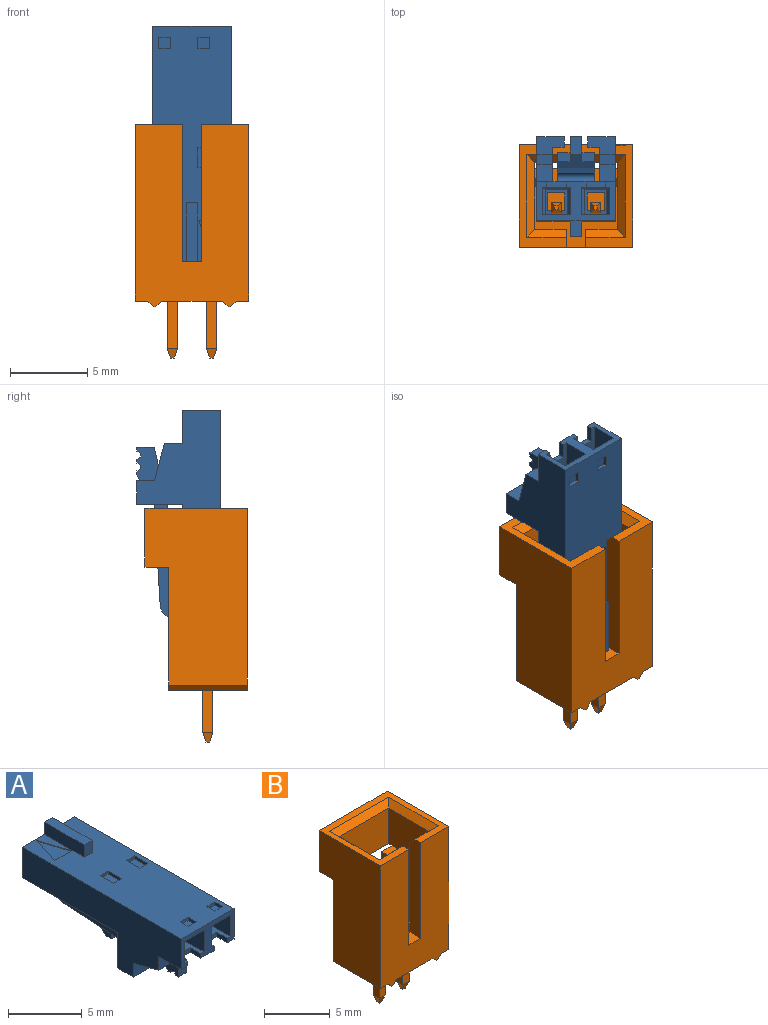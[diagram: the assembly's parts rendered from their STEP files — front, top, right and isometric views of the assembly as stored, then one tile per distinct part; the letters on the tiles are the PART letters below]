
ASSEMBLY  parts=2 mates=1
PART A: 129 faces, bbox 5.1x15.2x6.5 mm
  f0: plane 5.05x2.51mm, normal (0,-1,0), area 5.2mm2, adj f1,f2,f3,f4,f5,f32,f33,f34
  f1: plane 1.02x0.37mm, normal (1,0,0), area 0.4mm2, adj f0,f2,f38,f86
  f2: plane 8.38x1.85mm, normal (0,0,1), area 14.3mm2, adj f0,f1,f3,f5,f7,f86,f87
  f3: plane 8.38x1.78mm, normal (1,0,0), area 14.9mm2, adj f0,f2,f4,f8
  f4: plane 8.38x1.85mm, normal (0,0,-1), area 15.5mm2, adj f0,f3,f5,f9
  f5: plane 8.38x1.78mm, normal (-1,0,0), area 14.9mm2, adj f0,f2,f4,f6
  f6: plane 1.78x0.25mm, normal (-0.76,-0.65,0), area 0.6mm2, adj f5,f7,f9,f11
  f7: plane 1.85x0.25mm, normal (0,-0.29,0.96), area 0.4mm2, adj f2,f6,f8,f12
  f8: plane 1.78x0.25mm, normal (0.76,-0.65,0), area 0.6mm2, adj f3,f7,f9,f13
  f9: plane 1.85x0.25mm, normal (0,-0.29,-0.96), area 0.4mm2, adj f4,f6,f8,f10
  f10: plane 5.79x1.42mm, normal (0,0,-1), area 8.2mm2, adj f9,f11,f13,f14
  f11: plane 5.79x1.63mm, normal (-1,0,0), area 9.4mm2, adj f6,f10,f12,f14
  f12: plane 5.79x1.42mm, normal (0,0,1), area 8.2mm2, adj f7,f11,f13,f14
  f13: plane 5.79x1.63mm, normal (1,0,0), area 9.4mm2, adj f8,f10,f12,f14
  f14: plane 1.63x1.42mm, normal (0,-1,0), area 1.1mm2, adj f10,f11,f12,f13,f15,f16,f17,f18
  f15: plane 1.12x0.46mm, normal (1,0,0), area 0.5mm2, adj f14,f16,f18,f21
  f16: plane 1.12x0.46mm, normal (0,0,-1), area 0.5mm2, adj f14,f15,f17,f22
  f17: plane 1.12x0.46mm, normal (-1,0,0), area 0.5mm2, adj f14,f16,f18,f23
  f18: plane 1.12x0.46mm, normal (0,0,1), area 0.5mm2, adj f14,f15,f17,f19
  f19: plane 1.83x0.36mm, normal (0,0.71,0.71), area 0.7mm2, adj f18,f20,f21,f23
  f20: plane 5.05x3.53mm, normal (0,1,0), area 6.8mm2, adj f19,f21,f22,f23,f24,f25,f26,f27
  f21: plane 1.83x0.36mm, normal (0.71,0.71,0), area 0.7mm2, adj f15,f19,f20,f22
  f22: plane 1.83x0.36mm, normal (0,0.71,-0.71), area 0.7mm2, adj f16,f20,f21,f23
  f23: plane 1.83x0.36mm, normal (-0.71,0.71,0), area 0.7mm2, adj f17,f19,f20,f22
  f24: plane 1.83x0.36mm, normal (0.71,0.71,0), area 0.7mm2, adj f20,f25,f27,f126
  f25: plane 1.83x0.36mm, normal (0,0.71,0.71), area 0.7mm2, adj f20,f24,f26,f127
  f26: plane 1.83x0.36mm, normal (-0.71,0.71,0), area 0.7mm2, adj f20,f25,f27,f128
  f27: plane 1.83x0.36mm, normal (0,0.71,-0.71), area 0.7mm2, adj f20,f24,f26,f28
  f28: plane 1.12x0.46mm, normal (0,0,-1), area 0.5mm2, adj f27,f29,f126,f128
  f29: plane 1.63x1.42mm, normal (0,-1,0), area 1.1mm2, adj f28,f30,f121,f122,f125,f126,f127,f128
  f30: plane 5.79x1.63mm, normal (1,0,0), area 9.4mm2, adj f29,f31,f121,f125
  f31: plane 1.78x0.25mm, normal (0.76,-0.65,0), area 0.6mm2, adj f30,f32,f120,f124
  f32: plane 8.38x1.78mm, normal (1,0,0), area 14.9mm2, adj f0,f31,f33,f35
  f33: plane 8.38x1.85mm, normal (0,0,-1), area 15.5mm2, adj f0,f32,f34,f124
  f34: plane 8.38x1.78mm, normal (-1,0,0), area 14.9mm2, adj f0,f33,f35,f123
  f35: plane 8.38x1.85mm, normal (0,0,1), area 14.3mm2, adj f0,f32,f34,f36,f37,f88,f120
  f36: plane 1.02x0.37mm, normal (1,0,0), area 0.4mm2, adj f0,f35,f37,f38
  f37: plane 1.27x0.37mm, normal (0,-1,0), area 0.5mm2, adj f35,f36,f38,f88
  f38: plane 15.24x5.05mm, normal (0,0,-1), area 63.2mm2, adj f0,f1,f20,f36,f37,f39,f41,f45
  f39: plane 3.94x2.24mm, normal (1,0,0), area 6.9mm2, adj f38,f40,f41,f43,f46,f47
  f40: plane 1.52x0.77mm, normal (0,0,1), area 1.2mm2, adj f39,f41,f43,f44
  f41: plane 2.92x1.77mm, normal (0,1,0), area 3.4mm2, adj f38,f39,f40,f42,f44,f45
  f42: plane 1.77x1.52mm, normal (0,0,-1), area 2.7mm2, adj f41,f43,f44,f45
  f43: plane 1.77x1.14mm, normal (0,-1,0), area 1.7mm2, adj f39,f40,f42,f44,f45,f47
  f44: plane 1.52x0.69mm, normal (1,0,0), area 1mm2, adj f40,f41,f42,f43
  f45: plane 15.24x5.44mm, normal (-1,0,0), area 46.3mm2, adj f0,f20,f38,f41,f42,f43,f46,f47
  f46: plane 1.14x0.99mm, normal (0,-1,0), area 1.1mm2, adj f38,f39,f45,f47
  f47: plane 2.41x0.99mm, normal (0,-0.25,-0.97), area 2.5mm2, adj f39,f43,f45,f46
  f48: plane 15.24x5.05mm, normal (0,0,1), area 69mm2, adj f0,f20,f45,f49,f50,f51,f52,f55
  f49: plane 0.76x0.25mm, normal (0,1,0), area 0.2mm2, adj f48,f50,f52,f53
  f50: plane 1.27x0.25mm, normal (1,0,0), area 0.3mm2, adj f48,f49,f51,f53
  f51: plane 0.76x0.25mm, normal (0,-1,0), area 0.2mm2, adj f48,f50,f52,f53
  f52: plane 1.27x0.25mm, normal (-1,0,0), area 0.3mm2, adj f48,f49,f51,f53
  f53: plane 1.27x0.76mm, normal (0,0,1), area 1mm2, adj f49,f50,f51,f52
  f54: plane 0.76x0.76mm, normal (0,0,1), area 0.6mm2, adj f55,f56,f57,f58
  f55: plane 0.76x0.25mm, normal (0,1,0), area 0.2mm2, adj f48,f54,f56,f58
  f56: plane 0.76x0.25mm, normal (1,0,0), area 0.2mm2, adj f48,f54,f55,f57
  f57: plane 0.76x0.25mm, normal (0,-1,0), area 0.2mm2, adj f48,f54,f56,f58
  f58: plane 0.76x0.25mm, normal (-1,0,0), area 0.2mm2, adj f48,f54,f55,f57
  f59: plane 0.76x0.25mm, normal (0,1,0), area 0.2mm2, adj f48,f60,f62,f63
  f60: plane 1.27x0.25mm, normal (1,0,0), area 0.3mm2, adj f48,f59,f61,f63
  f61: plane 0.76x0.25mm, normal (0,-1,0), area 0.2mm2, adj f48,f60,f62,f63
  f62: plane 1.27x0.25mm, normal (-1,0,0), area 0.3mm2, adj f48,f59,f61,f63
  f63: plane 1.27x0.76mm, normal (0,0,1), area 1mm2, adj f59,f60,f61,f62
  f64: plane 0.76x0.76mm, normal (0,0,1), area 0.6mm2, adj f65,f66,f67,f68
  f65: plane 0.76x0.25mm, normal (0,1,0), area 0.2mm2, adj f48,f64,f66,f68
  f66: plane 0.76x0.25mm, normal (1,0,0), area 0.2mm2, adj f48,f64,f65,f67
  f67: plane 0.76x0.25mm, normal (0,-1,0), area 0.2mm2, adj f48,f64,f66,f68
  f68: plane 0.76x0.25mm, normal (-1,0,0), area 0.2mm2, adj f48,f64,f65,f67
  f69: plane 3.81x1.02mm, normal (1,0,0), area 3.9mm2, adj f20,f48,f70,f72
  f70: plane 1.02x0.76mm, normal (0,-1,0), area 0.8mm2, adj f48,f69,f71,f72
  f71: plane 3.81x1.02mm, normal (-1,0,0), area 3.9mm2, adj f20,f48,f70,f72
  f72: plane 3.81x0.76mm, normal (0,0,1), area 2.9mm2, adj f20,f69,f70,f71
  f73: plane 15.24x5.44mm, normal (1,0,0), area 46.3mm2, adj f0,f20,f38,f48,f74,f77,f78,f80
  f74: plane 2.92x1.77mm, normal (0,1,0), area 3.4mm2, adj f38,f73,f75,f76,f78,f79
  f75: plane 3.94x2.24mm, normal (-1,0,0), area 6.9mm2, adj f38,f74,f76,f77,f80,f81
  f76: plane 1.52x0.77mm, normal (0,0,1), area 1.2mm2, adj f74,f75,f77,f79
  f77: plane 1.77x1.14mm, normal (0,-1,0), area 1.7mm2, adj f73,f75,f76,f78,f79,f80
  f78: plane 1.77x1.52mm, normal (0,0,-1), area 2.7mm2, adj f73,f74,f77,f79
  f79: plane 1.52x0.69mm, normal (-1,0,0), area 1mm2, adj f74,f76,f77,f78
  f80: plane 2.41x0.99mm, normal (0,-0.25,-0.97), area 2.5mm2, adj f73,f75,f77,f81
  f81: plane 1.14x0.99mm, normal (0,-1,0), area 1.1mm2, adj f38,f73,f75,f80
  f82: plane 2.54x0.81mm, normal (0.95,-0.3,0), area 0.1mm2, adj f48,f83,f84,f85
  f83: plane 2.54x0.81mm, normal (-0.95,-0.3,0), area 0.1mm2, adj f48,f82,f84,f85
  f84: plane 1.63x0.05mm, normal (0,1,0), area 0.1mm2, adj f48,f82,f83,f85
  f85: plane 2.54x1.63mm, normal (0,0,1), area 2.1mm2, adj f82,f83,f84
  f86: plane 1.27x0.37mm, normal (0,-1,0), area 0.5mm2, adj f1,f2,f38,f87
  f87: plane 1.02x0.37mm, normal (-1,0,0), area 0.4mm2, adj f0,f2,f38,f86
  f88: plane 1.02x0.37mm, normal (-1,0,0), area 0.4mm2, adj f0,f35,f37,f38
  f89: plane 8.84x1.89mm, normal (-1,0,0), area 7.8mm2, adj f38,f90,f92,f94,f110,f111,f113,f114
  f90: plane 8.07x2.44mm, normal (0,0.06,-1), area 16.1mm2, adj f89,f91,f92,f93,f95,f96,f112,f114
  f91: plane 3.68x1.62mm, normal (-1,0,0), area 4.4mm2, adj f90,f92,f94,f96,f97,f98,f99,f100
  f92: plane 0.84x0.58mm, normal (0,-1,0), area 0.5mm2, adj f89,f90,f91,f94
  f93: plane 0.84x0.58mm, normal (0,-1,0), area 0.5mm2, adj f90,f94,f95,f112
  f94: plane 3.68x2.44mm, normal (0,-0.22,0.98), area 5.5mm2, adj f89,f91,f92,f93,f95,f109,f110,f112
  f95: plane 3.68x1.62mm, normal (1,0,0), area 4.4mm2, adj f90,f93,f94,f96,f97,f98,f99,f100
  f96: plane 1.12x0.76mm, normal (0,1,0), area 0.9mm2, adj f90,f91,f95,f97
  f97: plane 1.52x0.76mm, normal (0,0,-1), area 1.2mm2, adj f91,f95,f96,f98
  f98: plane 0.76x0.19mm, normal (0,-1,0), area 0.1mm2, adj f91,f95,f97,f99
  f99: plane 0.76x0.38mm, normal (0,0.45,-0.89), area 0.3mm2, adj f91,f95,f98,f100
  f100: plane 0.76x0.25mm, normal (0,0,-1), area 0.2mm2, adj f91,f95,f99,f101
  f101: plane 0.76x0.25mm, normal (0,-0.89,-0.45), area 0.2mm2, adj f91,f95,f100,f102
  f102: plane 0.76x0.25mm, normal (0,0,-1), area 0.2mm2, adj f91,f95,f101,f103
  f103: plane 0.76x0.25mm, normal (0,0.89,-0.45), area 0.2mm2, adj f91,f95,f102,f104
  f104: plane 0.76x0.25mm, normal (0,0,-1), area 0.2mm2, adj f91,f95,f103,f105
  f105: plane 0.76x0.25mm, normal (0,-0.89,-0.45), area 0.2mm2, adj f91,f95,f104,f106
  f106: plane 0.76x0.25mm, normal (0,0,-1), area 0.2mm2, adj f91,f95,f105,f107
  f107: plane 0.76x0.25mm, normal (0,0.89,-0.45), area 0.2mm2, adj f91,f95,f106,f108
  f108: plane 0.76x0.25mm, normal (0,0,-1), area 0.2mm2, adj f91,f95,f107,f109
  f109: plane 1.13x0.76mm, normal (0,-1,0), area 0.9mm2, adj f91,f94,f95,f108
  f110: plane 5.94x2.44mm, normal (0,-0.06,1), area 14.5mm2, adj f89,f94,f111,f112
  f111: cylinder r=0.3mm len=2.44mm, axis (1,0,0), area 2.3mm2, adj f38,f89,f110,f112
  f112: plane 8.84x1.89mm, normal (1,0,0), area 7.8mm2, adj f38,f90,f93,f94,f110,f111,f113,f114
  f113: plane 2.44x0.6mm, normal (0,1,0), area 1.5mm2, adj f38,f89,f112,f114
  f114: cylinder r=0.81mm len=2.44mm, axis (1,0,0), area 3mm2, adj f89,f90,f112,f113
  f115: plane 2.03x0.64mm, normal (0,-1,0), area 1.3mm2, adj f90,f116,f118,f119
  f116: plane 1.22x0.71mm, normal (1,0,0), area 0.6mm2, adj f90,f115,f117,f119
  f117: plane 2.03x0.71mm, normal (0,0.73,-0.68), area 2mm2, adj f90,f116,f118,f119
  f118: plane 1.22x0.71mm, normal (-1,0,0), area 0.6mm2, adj f90,f115,f117,f119
  f119: plane 2.03x0.56mm, normal (0,0,-1), area 1.1mm2, adj f115,f116,f117,f118
  f120: plane 1.85x0.25mm, normal (0,-0.29,0.96), area 0.4mm2, adj f31,f35,f121,f123
  f121: plane 5.79x1.42mm, normal (0,0,1), area 8.2mm2, adj f29,f30,f120,f122
  f122: plane 5.79x1.63mm, normal (-1,0,0), area 9.4mm2, adj f29,f121,f123,f125
  f123: plane 1.78x0.25mm, normal (-0.76,-0.65,0), area 0.6mm2, adj f34,f120,f122,f124
  f124: plane 1.85x0.25mm, normal (0,-0.29,-0.96), area 0.4mm2, adj f31,f33,f123,f125
  f125: plane 5.79x1.42mm, normal (0,0,-1), area 8.2mm2, adj f29,f30,f122,f124
  f126: plane 1.12x0.46mm, normal (1,0,0), area 0.5mm2, adj f24,f28,f29,f127
  f127: plane 1.12x0.46mm, normal (0,0,1), area 0.5mm2, adj f25,f29,f126,f128
  f128: plane 1.12x0.46mm, normal (-1,0,0), area 0.5mm2, adj f26,f28,f29,f127
PART B: 76 faces, bbox 7.4x6.6x15.1 mm
  f0: plane 11.43x6.6mm, normal (-1,0,0), area 63.9mm2, adj f1,f2,f7,f12,f15,f17
  f1: plane 11.81x7.37mm, normal (0,-1,0), area 73.3mm2, adj f0,f2,f3,f4,f5,f6,f8,f9
  f2: plane 5.08x0.83mm, normal (0,0,-1), area 4.2mm2, adj f0,f1,f5,f7
  f3: plane 5.08x3.94mm, normal (0,0,-1), area 19.1mm2, adj f1,f7,f8,f40,f42,f48,f50,f58
  f4: plane 5.08x0.83mm, normal (0,0,-1), area 4.2mm2, adj f1,f7,f10,f11
  f5: plane 5.08x0.38mm, normal (-0.71,0,-0.71), area 2.7mm2, adj f1,f2,f6,f7
  f6: plane 5.08x0.13mm, normal (0,0,-1), area 0.6mm2, adj f1,f5,f7,f75
  f7: plane 8x7.37mm, normal (0,1,0), area 41mm2, adj f0,f2,f3,f4,f5,f6,f8,f9
  f8: plane 5.08x0.38mm, normal (-0.71,0,-0.71), area 2.7mm2, adj f1,f3,f7,f9
  f9: plane 5.08x0.13mm, normal (0,0,-1), area 0.6mm2, adj f1,f7,f8,f10
  f10: plane 5.08x0.38mm, normal (0.71,0,-0.71), area 2.7mm2, adj f1,f4,f7,f9
  f11: plane 11.43x6.6mm, normal (1,0,0), area 63.9mm2, adj f1,f4,f7,f12,f15,f17
  f12: plane 7.37x6.6mm, normal (0,0,1), area 13.9mm2, adj f0,f1,f11,f13,f14,f15,f16,f25
  f13: plane 3.05x1.27mm, normal (0,1,0), area 1.9mm2, adj f12,f14,f16
  f14: plane 3.05x0.64mm, normal (0.98,0,0.2), area 0.1mm2, adj f12,f13,f15,f16
  f15: plane 7.37x3.81mm, normal (0,1,0), area 26.1mm2, adj f0,f11,f12,f14,f16,f17
  f16: plane 3.05x0.64mm, normal (-0.98,0,0.2), area 0.1mm2, adj f12,f13,f14,f15
  f17: plane 7.37x1.52mm, normal (0,0,-1), area 9.2mm2, adj f0,f7,f11,f15,f18,f23,f24
  f18: plane 8.38x4.32mm, normal (1,0,0), area 28.6mm2, adj f17,f20,f24,f30,f31,f35,f36,f37
  f19: plane 1.14x0.64mm, normal (0,0,1), area 0.7mm2, adj f7,f21,f23,f32
  f20: plane 1.14x0.64mm, normal (0,0,1), area 0.7mm2, adj f7,f18,f37,f38
  f21: plane 1.14x0.51mm, normal (0,-0.71,0.71), area 0.8mm2, adj f19,f22,f23,f32
  f22: plane 4.57x1.14mm, normal (0,-1,0), area 5.2mm2, adj f21,f23,f31,f32
  f23: plane 8.38x4.32mm, normal (-1,0,0), area 28.6mm2, adj f17,f19,f21,f22,f24,f26,f29,f31
  f24: plane 5.33x3.3mm, normal (0,-1,0), area 17.6mm2, adj f17,f18,f23,f25
  f25: plane 6.35x0.51mm, normal (0,-0.71,0.71), area 4.2mm2, adj f12,f24,f26,f35
  f26: plane 5.33x0.51mm, normal (-0.71,0,0.71), area 3.5mm2, adj f12,f23,f25,f27
  f27: plane 2.54x0.51mm, normal (0,0.71,0.71), area 1.6mm2, adj f12,f26,f28,f29
  f28: plane 8.89x1.14mm, normal (-1,0,0), area 10mm2, adj f1,f12,f27,f29,f31
  f29: plane 8.38x2.03mm, normal (0,1,0), area 17mm2, adj f23,f27,f28,f31
  f30: plane 8.38x2.03mm, normal (0,1,0), area 17mm2, adj f18,f31,f33,f34
  f31: plane 5.33x5.08mm, normal (0,0,1), area 19mm2, adj f1,f7,f18,f22,f23,f28,f29,f30
  f32: plane 5.08x1.14mm, normal (-1,0,0), area 5.7mm2, adj f7,f19,f21,f22,f31
  f33: plane 8.89x1.14mm, normal (1,0,0), area 10mm2, adj f1,f12,f30,f31,f34
  f34: plane 2.54x0.51mm, normal (0,0.71,0.71), area 1.6mm2, adj f12,f30,f33,f35
  f35: plane 5.33x0.51mm, normal (0.71,0,0.71), area 3.5mm2, adj f12,f18,f25,f34
  f36: plane 4.57x1.14mm, normal (0,-1,0), area 5.2mm2, adj f18,f31,f37,f38
  f37: plane 1.14x0.51mm, normal (0,-0.71,0.71), area 0.8mm2, adj f18,f20,f36,f38
  f38: plane 5.08x1.14mm, normal (1,0,0), area 5.7mm2, adj f7,f20,f31,f36,f37
  f39: plane 5.46x0.66mm, normal (-1,0,0), area 3.6mm2, adj f31,f41,f47,f56
  f40: plane 3.05x0.66mm, normal (-1,0,0), area 2mm2, adj f3,f42,f48,f54
  f41: plane 5.46x0.66mm, normal (0,1,0), area 3.6mm2, adj f31,f39,f43,f49
  f42: plane 3.05x0.66mm, normal (0,1,0), area 2mm2, adj f3,f40,f50,f53
  f43: plane 0.66x0.64mm, normal (0,0.95,0.3), area 0.3mm2, adj f41,f44,f45,f56
  f44: plane 0.66x0.64mm, normal (0.95,0,0.3), area 0.3mm2, adj f43,f45,f46,f49
  f45: plane 0.25x0.25mm, normal (0,0,1), area 0.1mm2, adj f43,f44,f46,f56
  f46: plane 0.66x0.64mm, normal (0,-0.95,0.3), area 0.3mm2, adj f44,f45,f47,f56
  f47: plane 5.46x0.66mm, normal (0,-1,0), area 3.6mm2, adj f31,f39,f46,f49
  f48: plane 3.05x0.66mm, normal (0,-1,0), area 2mm2, adj f3,f40,f50,f55
  f49: plane 5.46x0.66mm, normal (1,0,0), area 3.6mm2, adj f31,f41,f44,f47
  f50: plane 3.05x0.66mm, normal (1,0,0), area 2mm2, adj f3,f42,f48,f51
  f51: plane 0.66x0.64mm, normal (0.95,0,-0.3), area 0.3mm2, adj f50,f52,f53,f55
  f52: plane 0.25x0.25mm, normal (0,0,-1), area 0.1mm2, adj f51,f53,f54,f55
  f53: plane 0.66x0.64mm, normal (0,0.95,-0.3), area 0.3mm2, adj f42,f51,f52,f54
  f54: plane 0.66x0.64mm, normal (-0.95,0,-0.3), area 0.3mm2, adj f40,f52,f53,f55
  f55: plane 0.66x0.64mm, normal (0,-0.95,-0.3), area 0.3mm2, adj f48,f51,f52,f54
  f56: plane 0.66x0.64mm, normal (-0.95,0,0.3), area 0.3mm2, adj f39,f43,f45,f46
  f57: plane 5.46x0.66mm, normal (-1,0,0), area 3.6mm2, adj f31,f59,f62,f68
  f58: plane 3.05x0.66mm, normal (-1,0,0), area 2mm2, adj f3,f63,f69,f74
  f59: plane 0.66x0.64mm, normal (-0.95,0,0.3), area 0.3mm2, adj f57,f60,f61,f67
  f60: plane 0.25x0.25mm, normal (0,0,1), area 0.1mm2, adj f59,f61,f66,f67
  f61: plane 0.66x0.64mm, normal (0,0.95,0.3), area 0.3mm2, adj f59,f60,f62,f66
  f62: plane 5.46x0.66mm, normal (0,1,0), area 3.6mm2, adj f31,f57,f61,f64
  f63: plane 3.05x0.66mm, normal (0,1,0), area 2mm2, adj f3,f58,f65,f73
  f64: plane 5.46x0.66mm, normal (1,0,0), area 3.6mm2, adj f31,f62,f66,f68
  f65: plane 3.05x0.66mm, normal (1,0,0), area 2mm2, adj f3,f63,f69,f71
  f66: plane 0.66x0.64mm, normal (0.95,0,0.3), area 0.3mm2, adj f60,f61,f64,f67
  f67: plane 0.66x0.64mm, normal (0,-0.95,0.3), area 0.3mm2, adj f59,f60,f66,f68
  f68: plane 5.46x0.66mm, normal (0,-1,0), area 3.6mm2, adj f31,f57,f64,f67
  f69: plane 3.05x0.66mm, normal (0,-1,0), area 2mm2, adj f3,f58,f65,f70
  f70: plane 0.66x0.64mm, normal (0,-0.95,-0.3), area 0.3mm2, adj f69,f71,f72,f74
  f71: plane 0.66x0.64mm, normal (0.95,0,-0.3), area 0.3mm2, adj f65,f70,f72,f73
  f72: plane 0.25x0.25mm, normal (0,0,-1), area 0.1mm2, adj f70,f71,f73,f74
  f73: plane 0.66x0.64mm, normal (0,0.95,-0.3), area 0.3mm2, adj f63,f71,f72,f74
  f74: plane 0.66x0.64mm, normal (-0.95,0,-0.3), area 0.3mm2, adj f58,f70,f72,f73
  f75: plane 5.08x0.38mm, normal (0.71,0,-0.71), area 2.7mm2, adj f1,f3,f6,f7
PLACE A rot(axis=(0,-0.71,0.71),180deg) t=(3.68,2.95,10.16)mm
PLACE B t=(3.68,2.54,7.62)mm
MATE fastened A.f20 <-> B.f31  axis (0,0,-1) through (3.68,2.75,2.54)mm
